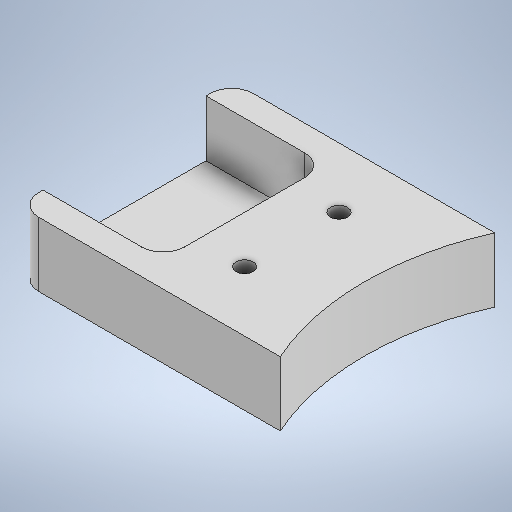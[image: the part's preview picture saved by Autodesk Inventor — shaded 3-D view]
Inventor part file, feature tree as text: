
AUTODESK INVENTOR PART (.ipt)
format: ipt  version: 2025 (Build 290162000, 162)  size: 272,384 bytes
history: native  units: mm
features: sketch x4, extrude x3, hole x1, fillet x1
ambient origin geometry x8: Origin, YZ Plane, XZ Plane, XY Plane, X Axis, Y Axis, Z Axis, Center Point
bodies: Solid1 (feature_tree)
feature tree (9):
  extrude  "Extrusion1"  Depth=15.0mm TaperAngle=0.0deg
  extrude  "Extrusion2"  Depth=38.0mm
  hole  "Hole1"  [1 undecoded]
  fillet  "Fillet1"  Radius=39.0mm
  extrude  "Extrusion3"  Depth=5.0mm
  sketch  "Sketch1"  dims[d0=85.0mm d1=61.0mm d2=235.0mm d4=15.0mm d5=0.0mm]
  sketch  "Sketch2"  dims[d6=5.0mm d7=38.0mm]
  sketch  "Sketch3"  dims[d8=28.0mm d9=13.1mm d10=0.0mm]
  sketch  "Sketch4"  dims[d11=4.0mm d12=6.0mm d13=8.0mm d14=6.0mm d15=90.0deg d16=3.0mm d17=0.0mm d19=39.0mm d22=11.0mm d23=5.0mm d24=123.0mm d25=0.0mm d26=0.0mm]
note: 1 required parameter value undecoded (feature->parameter linkage not recoverable at this tier; creation-order binding heuristic only, values carry confidence <= 0.55)
